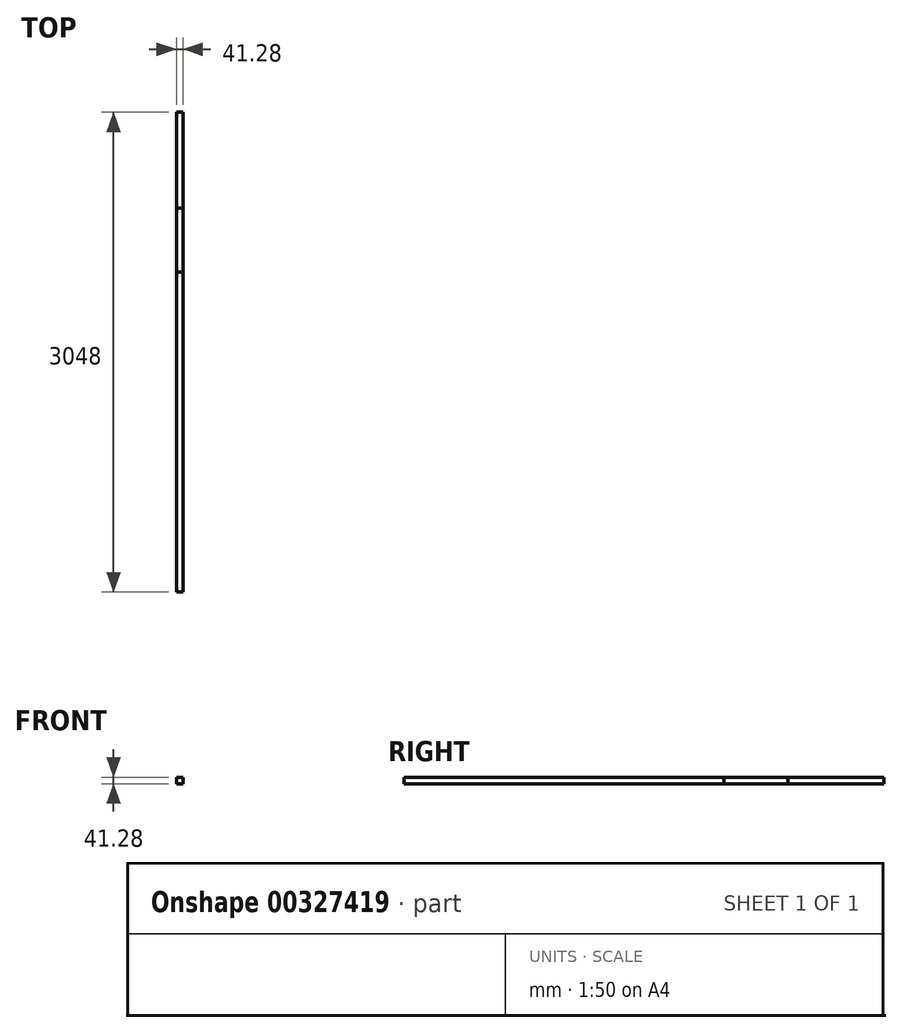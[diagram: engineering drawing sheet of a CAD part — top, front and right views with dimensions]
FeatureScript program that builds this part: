
annotation { "Feature Type Name" : "Feature", "Feature Type Description" : "" }
export const myFeature = defineFeature(function(context is Context, id is Id, definition is map)
    precondition{}
    {
        {
            var Q0;
            Q0=qCreatedBy(makeId("Front.planeOp"),FACE);
            var sketch = newSketch(context, id + "F0", { "sketchPlane" : qUnion([Q0])});
            skLineSegment(sketch, "E0.bottom", {"start": v(-20.64, 20.64) * mm, "end": v(20.64, 20.64) * mm});
            skLineSegment(sketch, "E0.top", {"start": v(-20.64, -20.64) * mm, "end": v(20.64, -20.64) * mm});
            skLineSegment(sketch, "E0.left", {"start": v(-20.64, 20.64) * mm, "end": v(-20.64, -20.64) * mm});
            skLineSegment(sketch, "E0.right", {"start": v(20.64, 20.64) * mm, "end": v(20.64, -20.64) * mm});
            skSolve(sketch);
        }
        {
            var Q0;
            Q0 = qSketchRegion(id + "F0", true);
            extrude(context, id + "F1", {"entities" : qUnion([Q0]), "depth" : 609.6 * mm, "offsetDistance" : 25.4 * mm});
        }
        {
            var Q0;
            Q0 = qSketchRegion(id + "F0", true);
            extrude(context, id + "F2", {"entities" : qUnion([Q0]), "depth" : 1016 * mm, "offsetDistance" : 25.4 * mm});
        }
        {
            var Q0;
            Q0 = qSketchRegion(id + "F0", true);
            extrude(context, id + "F3", {"entities" : qUnion([Q0]), "depth" : 3048 * mm, "offsetDistance" : 25.4 * mm});
        }
    });
